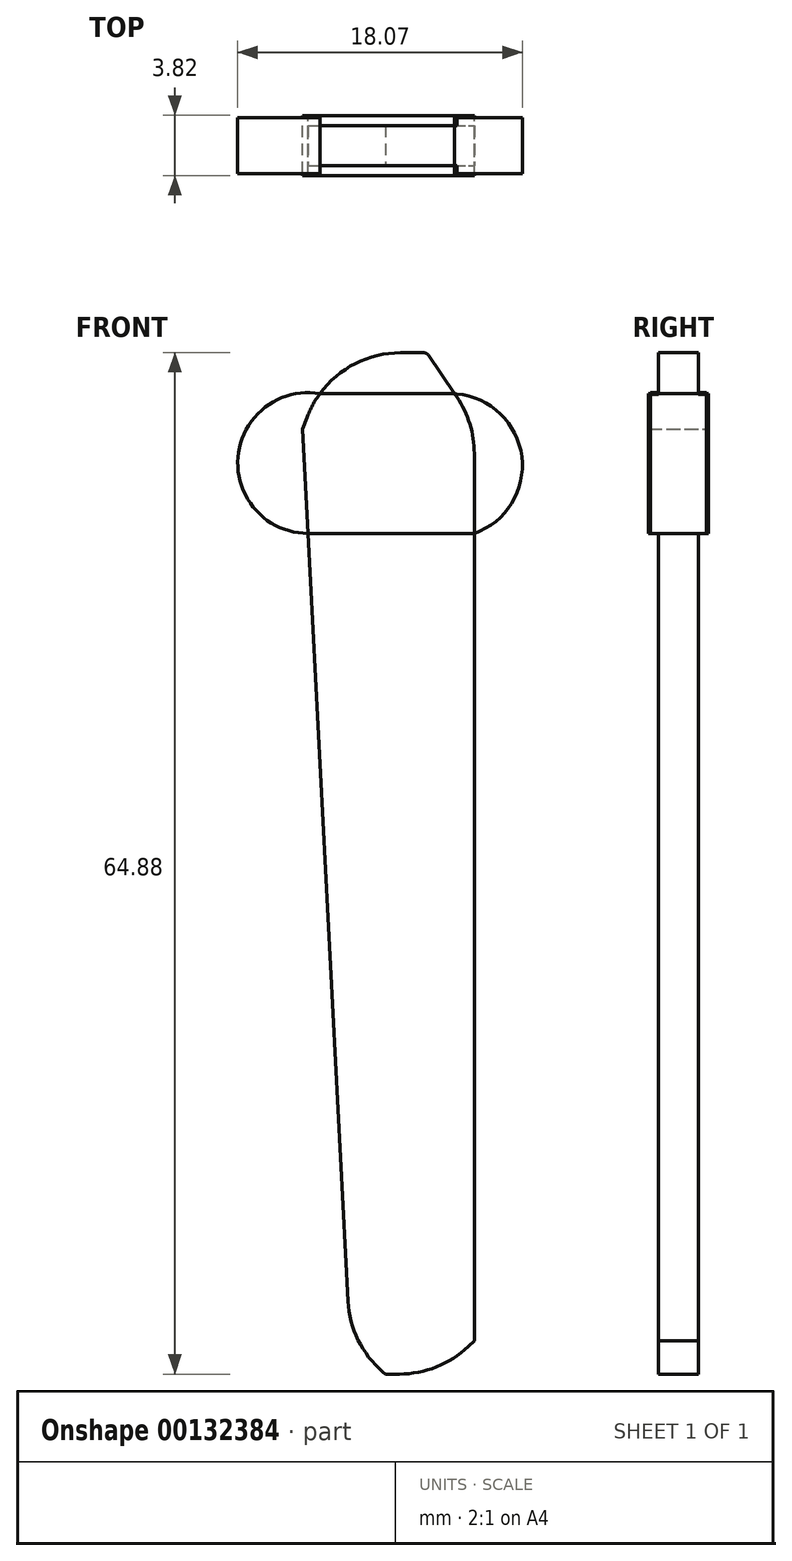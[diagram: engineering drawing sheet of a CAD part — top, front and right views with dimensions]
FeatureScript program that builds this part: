
annotation { "Feature Type Name" : "Feature", "Feature Type Description" : "" }
export const myFeature = defineFeature(function(context is Context, id is Id, definition is map)
    precondition{}
    {
        {
            var Q0;
            Q0=qCreatedBy(makeId("Front.planeOp"),FACE);
            var sketch = newSketch(context, id + "F0", { "sketchPlane" : qUnion([Q0])});
            skLineSegment(sketch, "E0", {"start": v(-26.84, 60.03) * mm, "end": v(-23.95, 4.62) * mm});
            skLineSegment(sketch, "E1", {"start": v(-21.76, 0.15) * mm, "end": v(-21.6, 0) * mm});
            skLineSegment(sketch, "E2", {"start": v(-21.6, 0) * mm, "end": v(-20.7, 0) * mm});
            skLineSegment(sketch, "E3", {"start": v(-16.32, 1.76) * mm, "end": v(-15.94, 2.12) * mm});
            skLineSegment(sketch, "E4", {"start": v(-15.94, 2.12) * mm, "end": v(-15.94, 58.48) * mm});
            skLineSegment(sketch, "E5", {"start": v(-17.04, 62.05) * mm, "end": v(-18.86, 64.72) * mm});
            skLineSegment(sketch, "E6", {"start": v(-19.15, 64.88) * mm, "end": v(-20.62, 64.88) * mm});
            skLineSegment(sketch, "E7", {"start": v(-26.57, 60.76) * mm, "end": v(-26.84, 60.03) * mm});
            skPoint(sketch, "E8.endSnap0", {"position": v(-17.45, 62.66) * mm});
            skPoint(sketch, "E9.visualSharp", {"position": v(-25.02, 64.88) * mm});
            skArc(sketch, "E9.filletArc", {"start": v(-20.62, 64.88) * mm, "mid": v(-24.24, 63.74) * mm, "end": v(-26.57, 60.76) * mm});
            skPoint(sketch, "E10.visualSharp", {"position": v(-15.94, 60.44) * mm});
            skArc(sketch, "E10.filletArc", {"start": v(-15.94, 58.48) * mm, "mid": v(-16.22, 60.35) * mm, "end": v(-17.04, 62.05) * mm});
            skPoint(sketch, "E11.visualSharp", {"position": v(-18.97, 64.88) * mm});
            skArc(sketch, "E11.filletArc", {"start": v(-18.86, 64.72) * mm, "mid": v(-18.99, 64.83) * mm, "end": v(-19.15, 64.88) * mm});
            skPoint(sketch, "E12.visualSharp", {"position": v(-18.16, 0) * mm});
            skArc(sketch, "E12.filletArc", {"start": v(-20.7, 0) * mm, "mid": v(-18.34, 0.46) * mm, "end": v(-16.32, 1.76) * mm});
            skPoint(sketch, "E13.visualSharp", {"position": v(-23.81, 1.92) * mm});
            skArc(sketch, "E13.filletArc", {"start": v(-23.95, 4.62) * mm, "mid": v(-23.31, 2.16) * mm, "end": v(-21.76, 0.15) * mm});
            skLineSegment(sketch, "E14", {"start": v(-26.5, 53.4) * mm, "end": v(-15.94, 53.4) * mm});
            skLineSegment(sketch, "E15", {"start": v(-25.75, 62.28) * mm, "end": v(-17.45, 62.28) * mm});
            skArc(sketch, "E16", {"start": v(-25.75, 62.28) * mm, "mid": v(-30.95, 58.24) * mm, "end": v(-26.5, 53.4) * mm});
            skArc(sketch, "E17", {"start": v(-15.94, 53.4) * mm, "mid": v(-12.95, 58.48) * mm, "end": v(-17.45, 62.28) * mm});
            skLineSegment(sketch, "E18", {"start": v(-26.5, 53.4) * mm, "end": v(-17.04, 62.26) * mm});
            skLineSegment(sketch, "E19", {"start": v(-25.75, 62.28) * mm, "end": v(-15.94, 53.4) * mm});
            skSolve(sketch);
        }
        {
            var Q0;
            {var subQ0=sQuery(id+"F0.wireOp",EDGE,"E17");var subQ1=sQuery(id+"F0.wireOp",EDGE,"E5");var subQ2=makeQuery(id+"F0.imprint","INTERSECT",VERTEX,{"derivedFrom":[subQ1,subQ0]});Q0=makeQuery(id+"F0.imprint","IMPRINT",FACE,{"disambiguationData":[TD([[makeQuery(id+"F0.imprint","IMPRINT",EDGE,{"disambiguationData":[TD([[subQ2,1.0]])],"derivedFrom":subQ1}),-1.0]])]});}
            var Q1;
            Q1=makeQuery(id+"F0.imprint","IMPRINT",FACE,{"disambiguationData":[TD([[makeQuery(id+"F0.imprint","IMPRINT",EDGE,{"derivedFrom":sQuery(id+"F0.wireOp",EDGE,"E1")}),1.0]])]});
            var Q2;
            {var subQ2=sQuery(id+"F0.wireOp",EDGE,"E6");Q2=makeQuery(id+"F0.imprint","IMPRINT",FACE,{"disambiguationData":[TD([[makeQuery(id+"F0.imprint","IMPRINT",EDGE,{"derivedFrom":subQ2}),1.0]])]});}
            extrude(context, id + "F1", {"entities" : qUnion([Q0, Q1, Q2]), "endBound" : BoundingType.SYMMETRIC, "oppositeDirection" : true, "depth" : 2.54 * mm});
        }
        {
            var Q0;
            {var subQ0=sQuery(id+"F0.wireOp",EDGE,"E7");Q0=makeQuery(id+"F0.imprint","IMPRINT",FACE,{"disambiguationData":[TD([[makeQuery(id+"F0.imprint","IMPRINT",EDGE,{"derivedFrom":subQ0}),-1.0]])]});}
            var Q1;
            {var subQ0=sQuery(id+"F0.wireOp",EDGE,"E10.filletArc");Q1=makeQuery(id+"F0.imprint","IMPRINT",FACE,{"disambiguationData":[TD([[makeQuery(id+"F0.imprint","IMPRINT",EDGE,{"derivedFrom":subQ0}),-1.0]])]});}
            extrude(context, id + "F2", {"entities" : qUnion([Q0, Q1]), "operationType" : NewBodyOperationType.ADD, "endBound" : BoundingType.SYMMETRIC, "depth" : 3.56 * mm});
        }
        {
            var Q0;
            {var subQ1=sQuery(id+"F0.wireOp",EDGE,"E7");Q0=makeQuery(id+"F0.imprint","IMPRINT",FACE,{"disambiguationData":[TD([[makeQuery(id+"F0.imprint","IMPRINT",EDGE,{"derivedFrom":subQ1}),1.0]])]});}
            var Q1;
            {var subQ1=sQuery(id+"F0.wireOp",EDGE,"E15");Q1=makeQuery(id+"F0.imprint","IMPRINT",FACE,{"disambiguationData":[TD([[makeQuery(id+"F0.imprint","IMPRINT",EDGE,{"derivedFrom":subQ1}),-1.0]])]});}
            var Q2;
            {var subQ0=sQuery(id+"F0.wireOp",EDGE,"E14");Q2=makeQuery(id+"F0.imprint","IMPRINT",FACE,{"disambiguationData":[TD([[makeQuery(id+"F0.imprint","IMPRINT",EDGE,{"derivedFrom":subQ0}),1.0]])]});}
            var Q3;
            {var subQ5=sQuery(id+"F0.wireOp",EDGE,"E10.filletArc");Q3=makeQuery(id+"F0.imprint","IMPRINT",FACE,{"disambiguationData":[TD([[makeQuery(id+"F0.imprint","IMPRINT",EDGE,{"derivedFrom":subQ5}),1.0]])]});}
            extrude(context, id + "F3", {"entities" : qUnion([Q0, Q1, Q2, Q3]), "endBound" : BoundingType.SYMMETRIC, "depth" : 3.8 * mm});
        }
    });
